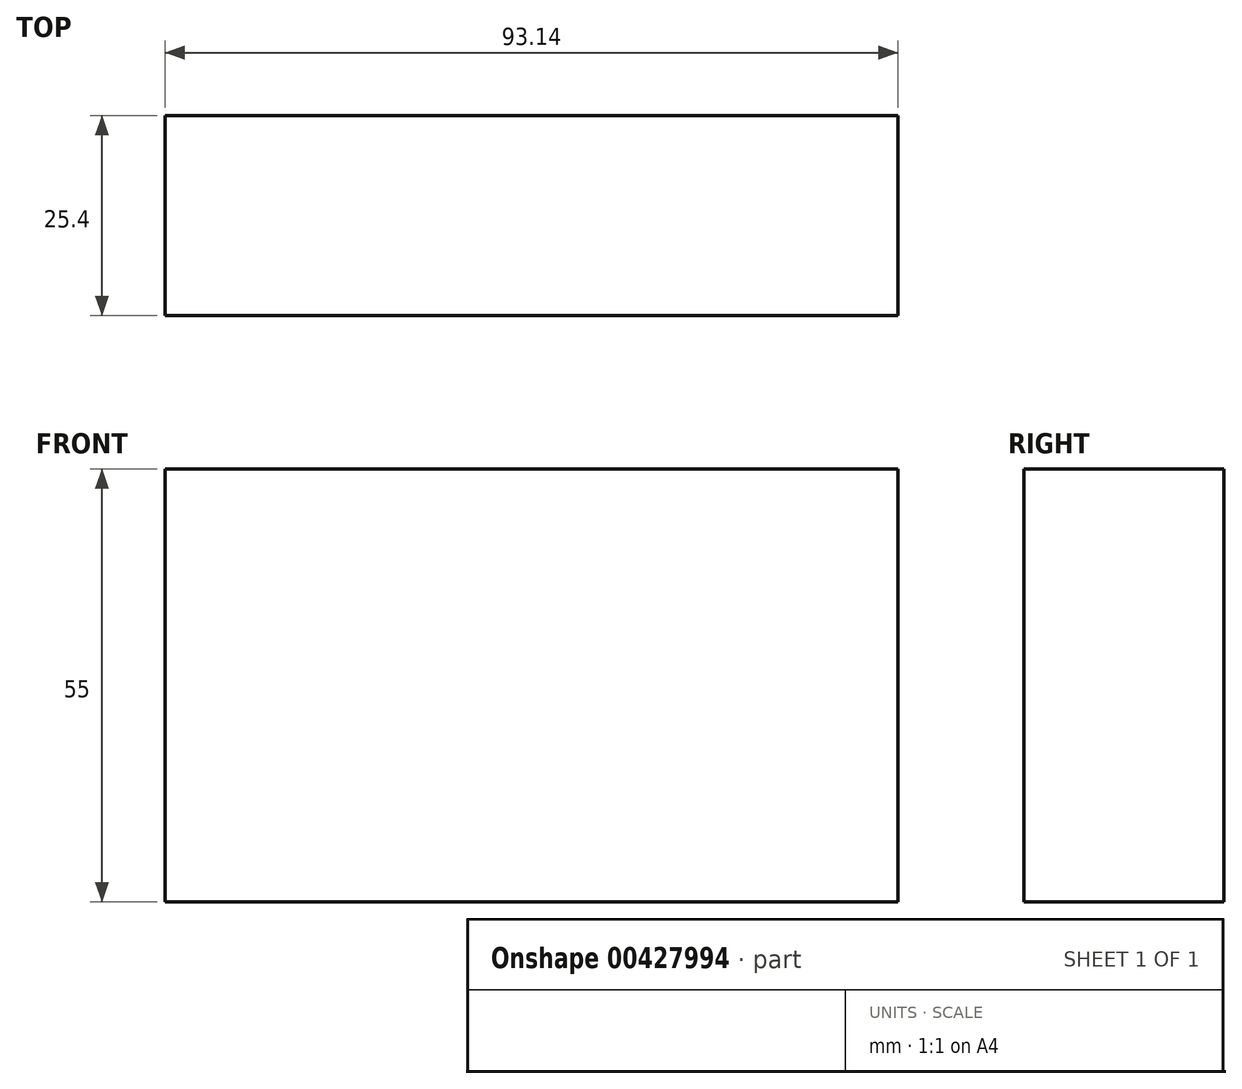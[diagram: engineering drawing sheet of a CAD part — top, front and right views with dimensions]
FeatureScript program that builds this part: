
annotation { "Feature Type Name" : "Feature", "Feature Type Description" : "" }
export const myFeature = defineFeature(function(context is Context, id is Id, definition is map)
    precondition{}
    {
        {
            var Q0;
            Q0=qCreatedBy(makeId("Front.planeOp"),FACE);
            var sketch = newSketch(context, id + "F0", { "sketchPlane" : qUnion([Q0])});
            skLineSegment(sketch, "E0.bottom", {"start": v(0, 0) * mm, "end": v(93.14, 0) * mm});
            skLineSegment(sketch, "E0.top", {"start": v(0, -55) * mm, "end": v(93.14, -55) * mm});
            skLineSegment(sketch, "E0.left", {"start": v(0, 0) * mm, "end": v(0, -55) * mm});
            skLineSegment(sketch, "E0.right", {"start": v(93.14, 0) * mm, "end": v(93.14, -55) * mm});
            skSolve(sketch);
        }
        {
            var Q0;
            Q0 = qSketchRegion(id + "F0", true);
            extrude(context, id + "F1", {"entities" : qUnion([Q0]), "depth" : 25.4 * mm});
        }
    });
